# Revit family: Safety & Protection_Bollard_UltiGroup_Steel Bollard
name_source: partatom
category: Generic Models
revit_build: Autodesk Revit Architecture 2016 (Build: 20150220_1215(x64)
units: mm (PartAtom-declared; Revit-internal decimal feet)

## family parameters
Always vertical = Yes
Can host rebar = No
Cut with Voids When Loaded = No
Host = Floor
OmniClass Number = 23.40.10.14.27
OmniClass Title = Bollards
Part Type = Normal
Room Calculation Point = No
Round Connector Dimension = Use Diameter
Shared = No
Work Plane-Based = No

## types (2) — shared parameters
Base Plate Length / 2 = 125 mm
Base Plate Thickness = 12 mm  [stored 0.0393701 ft]
Bollard Height = 1000 mm  [stored 3.28084 ft]
Bollard Radius = 70 mm
Fax = 07 846 2467
Fixing Hole = 95 mm
Manufacturer = UltiGroup
Powder Coated Yellow over Galvanized Steel = Powder Coated Yellow Over Galvanized Steel
Send Message = http://ultigroup.co.nz
Stainless Steel Bolts = Stainless Steel Bolts
URL = www.ultigroup.co.nz
zero-valued in all types: InstallationGroup_ANZRS, ModifiedIssue_ANZRS

## per-type parameters (varying)
| type | Description | Model | Surface Mount |
| Bollard - Cast in | Ulti Galvanized Steel Bollard - Cast In | GSBC1514 | No |
| Bollard - Surface Mount | Ulti Galvanized Steel Bollard - Surface Mount | GSBS1014 | Yes |

note: [stored X ft] marks values corroborated as IEEE doubles in the binary element streams (Revit-internal decimal feet)

## geometry (parser evidence)
native form markers: Sweep x1
no freeform markers — native parametric forms only
